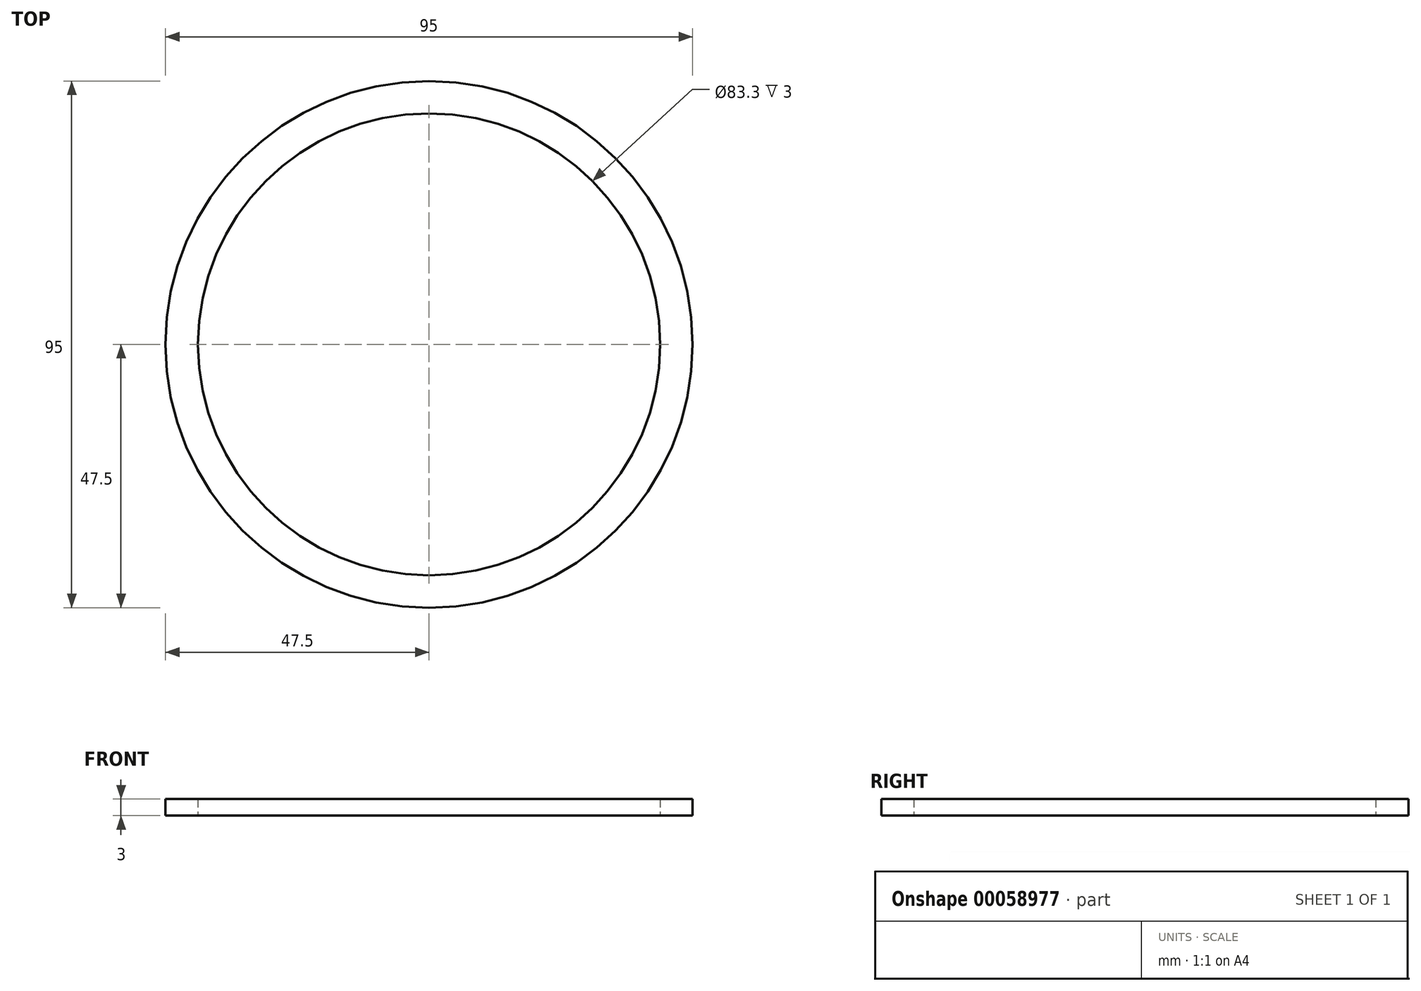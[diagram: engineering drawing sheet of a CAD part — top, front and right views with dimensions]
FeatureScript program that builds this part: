
annotation { "Feature Type Name" : "Feature", "Feature Type Description" : "" }
export const myFeature = defineFeature(function(context is Context, id is Id, definition is map)
    precondition{}
    {
        {
            var Q0;
            Q0=qCreatedBy(makeId("Top.planeOp"),FACE);
            var sketch = newSketch(context, id + "F0", { "sketchPlane" : qUnion([Q0])});
            skCircle(sketch, "E0", {"center": v(0, 0) * mm, "radius": 47.5 * mm});
            skCircle(sketch, "E1", {"center": v(0, 0) * mm, "radius": 41.65 * mm});
            skSolve(sketch);
        }
        {
            var Q0;
            Q0=makeQuery(id+"F0.imprint","IMPRINT",FACE,{"disambiguationData":[TD([[makeQuery(id+"F0.imprint","IMPRINT",EDGE,{"derivedFrom":sQuery(id+"F0.wireOp",EDGE,"E0")}),1.0]])]});
            extrude(context, id + "F1", {"entities" : qUnion([Q0]), "depth" : 3 * mm});
        }
    });
